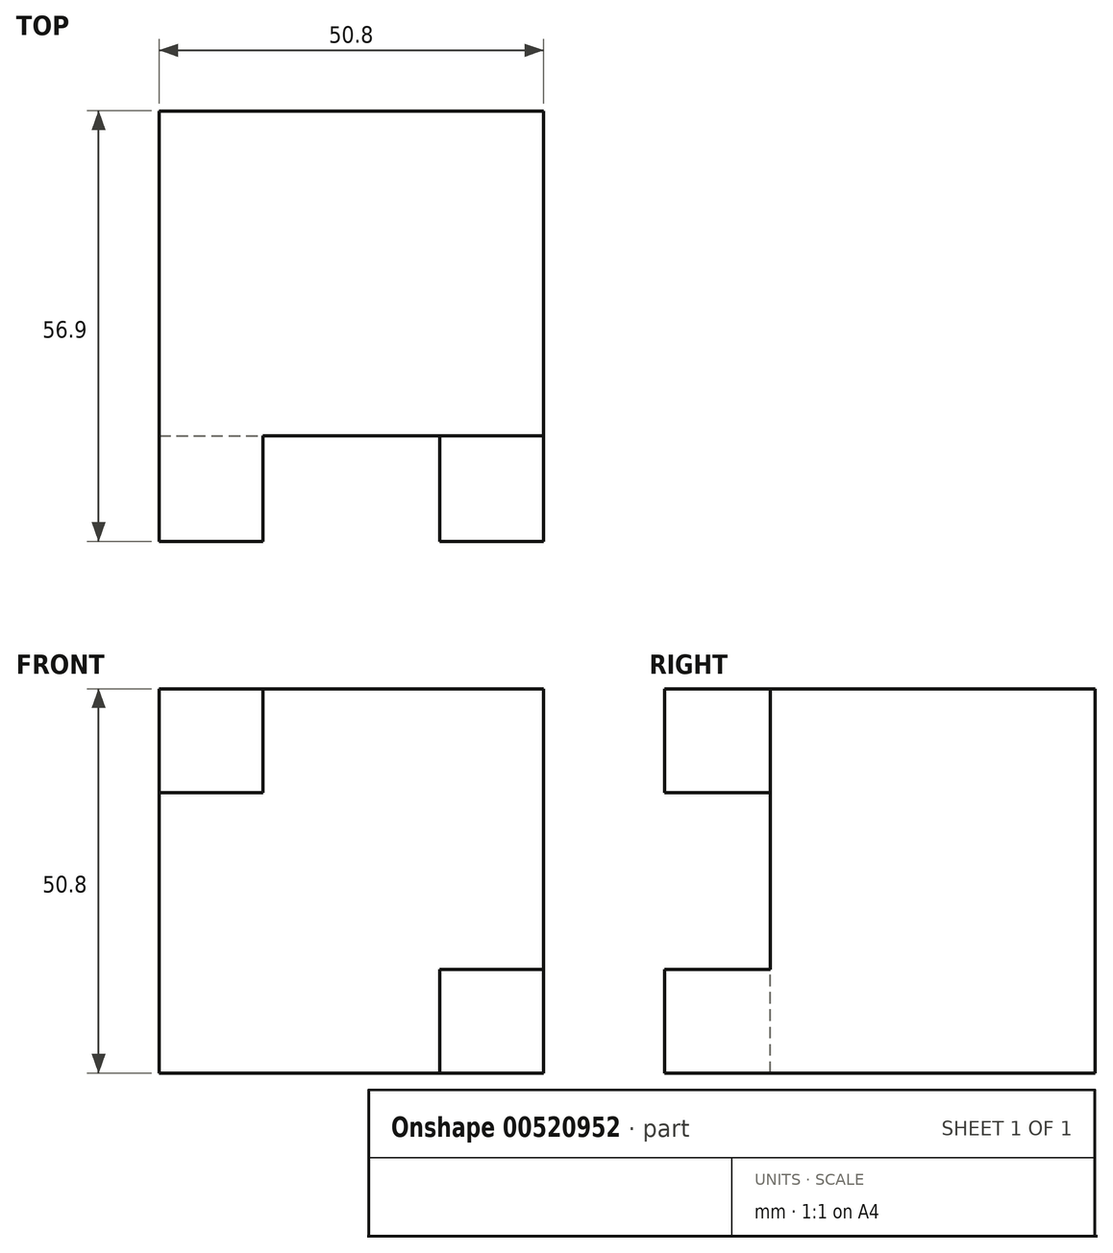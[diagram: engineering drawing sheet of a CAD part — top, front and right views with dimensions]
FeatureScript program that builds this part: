
annotation { "Feature Type Name" : "Feature", "Feature Type Description" : "" }
export const myFeature = defineFeature(function(context is Context, id is Id, definition is map)
    precondition{}
    {
        {
            var Q0;
            Q0=qCreatedBy(makeId("Front.planeOp"),FACE);
            var sketch = newSketch(context, id + "F0", { "sketchPlane" : qUnion([Q0])});
            skLineSegment(sketch, "E0.bottom", {"start": v(0, 0) * mm, "end": v(-50.8, 0) * mm});
            skLineSegment(sketch, "E0.top", {"start": v(0, 50.8) * mm, "end": v(-50.8, 50.8) * mm});
            skLineSegment(sketch, "E0.left", {"start": v(0, 0) * mm, "end": v(0, 50.8) * mm});
            skLineSegment(sketch, "E0.right", {"start": v(-50.8, 0) * mm, "end": v(-50.8, 50.8) * mm});
            skSolve(sketch);
        }
        {
            var Q0;
            Q0=makeQuery(id+"F0.imprint","IMPRINT",FACE,{"disambiguationData":[TD([[makeQuery(id+"F0.imprint","IMPRINT",EDGE,{"derivedFrom":sQuery(id+"F0.wireOp",EDGE,"E0.bottom")}),-1.0]])]});
            extrude(context, id + "F1", {"entities" : qUnion([Q0]), "oppositeDirection" : true, "depth" : 24.9 * mm, "offsetDistance" : 25.4 * mm});
        }
        {
            var Q0;
            Q0=makeQuery(id+"F1.opExtrude","CAP_FACE",FACE,{"disambiguationData":[OSD([sQuery(id+"F0.wireOp",EDGE,"E0.bottom"),sQuery(id+"F0.wireOp",EDGE,"E0.top"),sQuery(id+"F0.wireOp",EDGE,"E0.left"),sQuery(id+"F0.wireOp",EDGE,"E0.right")])],"isStart":true});
            var sketch = newSketch(context, id + "F2", { "sketchPlane" : qUnion([Q0])});
            skLineSegment(sketch, "E1.bottom", {"start": v(-50.8, 50.8) * mm, "end": v(-37.08, 50.8) * mm});
            skLineSegment(sketch, "E1.top", {"start": v(-50.8, 37.08) * mm, "end": v(-37.08, 37.08) * mm});
            skLineSegment(sketch, "E1.left", {"start": v(-50.8, 50.8) * mm, "end": v(-50.8, 37.08) * mm});
            skLineSegment(sketch, "E1.right", {"start": v(-37.08, 50.8) * mm, "end": v(-37.08, 37.08) * mm});
            skLineSegment(sketch, "E2.bottom", {"start": v(0, 0) * mm, "end": v(-13.72, 0) * mm});
            skLineSegment(sketch, "E2.top", {"start": v(0, 13.72) * mm, "end": v(-13.72, 13.72) * mm});
            skLineSegment(sketch, "E2.left", {"start": v(0, 0) * mm, "end": v(0, 13.72) * mm});
            skLineSegment(sketch, "E2.right", {"start": v(-13.72, 0) * mm, "end": v(-13.72, 13.72) * mm});
            skSolve(sketch);
        }
        {
            var Q0;
            Q0=makeQuery(id+"F2.imprint","IMPRINT",FACE,{"disambiguationData":[TD([[makeQuery(id+"F2.imprint","IMPRINT",EDGE,{"derivedFrom":sQuery(id+"F2.wireOp",EDGE,"E1.bottom")}),1.0]])]});
            var Q1;
            Q1=makeQuery(id+"F2.imprint","IMPRINT",FACE,{"disambiguationData":[TD([[makeQuery(id+"F2.imprint","IMPRINT",EDGE,{"derivedFrom":sQuery(id+"F2.wireOp",EDGE,"E2.bottom")}),-1.0]])]});
            extrude(context, id + "F3", {"entities" : qUnion([Q0, Q1]), "operationType" : NewBodyOperationType.ADD, "depth" : 13.97 * mm, "offsetDistance" : 25.4 * mm});
        }
        {
            var Q0;
            Q0=makeQuery(id+"F1.opExtrude","CAP_FACE",FACE,{"disambiguationData":[OSD([sQuery(id+"F0.wireOp",EDGE,"E0.bottom"),sQuery(id+"F0.wireOp",EDGE,"E0.top"),sQuery(id+"F0.wireOp",EDGE,"E0.left"),sQuery(id+"F0.wireOp",EDGE,"E0.right")])],"isStart":false});
            var sketch = newSketch(context, id + "F4", { "sketchPlane" : qUnion([Q0])});
            skLineSegment(sketch, "E3.bottom", {"start": v(50.8, 0) * mm, "end": v(37.08, 0) * mm});
            skLineSegment(sketch, "E3.top", {"start": v(50.8, 13.55) * mm, "end": v(37.08, 13.55) * mm});
            skLineSegment(sketch, "E3.left", {"start": v(50.8, 0) * mm, "end": v(50.8, 13.55) * mm});
            skLineSegment(sketch, "E3.right", {"start": v(37.08, 0) * mm, "end": v(37.08, 13.55) * mm});
            skLineSegment(sketch, "E4.bottom", {"start": v(50.8, 50.8) * mm, "end": v(37.08, 50.8) * mm});
            skLineSegment(sketch, "E4.top", {"start": v(50.8, 36.31) * mm, "end": v(37.08, 36.31) * mm});
            skLineSegment(sketch, "E4.left", {"start": v(50.8, 50.8) * mm, "end": v(50.8, 36.31) * mm});
            skLineSegment(sketch, "E4.right", {"start": v(37.08, 50.8) * mm, "end": v(37.08, 36.31) * mm});
            skLineSegment(sketch, "E5.bottom", {"start": v(0, 0) * mm, "end": v(13.72, 0) * mm});
            skLineSegment(sketch, "E5.top", {"start": v(0, 12.96) * mm, "end": v(13.72, 12.96) * mm});
            skLineSegment(sketch, "E5.left", {"start": v(0, 0) * mm, "end": v(0, 12.96) * mm});
            skLineSegment(sketch, "E5.right", {"start": v(13.72, 0) * mm, "end": v(13.72, 12.96) * mm});
            skLineSegment(sketch, "E6.bottom", {"start": v(0, 50.8) * mm, "end": v(13.72, 50.8) * mm});
            skLineSegment(sketch, "E6.top", {"start": v(0, 35.15) * mm, "end": v(13.72, 35.15) * mm});
            skLineSegment(sketch, "E6.left", {"start": v(0, 50.8) * mm, "end": v(0, 35.15) * mm});
            skLineSegment(sketch, "E6.right", {"start": v(13.72, 50.8) * mm, "end": v(13.72, 35.15) * mm});
            skSolve(sketch);
        }
        {
            var Q0;
            Q0=makeQuery(id+"F1.opExtrude","CAP_FACE",FACE,{"disambiguationData":[OSD([sQuery(id+"F0.wireOp",EDGE,"E0.bottom"),sQuery(id+"F0.wireOp",EDGE,"E0.top"),sQuery(id+"F0.wireOp",EDGE,"E0.left"),sQuery(id+"F0.wireOp",EDGE,"E0.right")])],"isStart":false});
            var sketch = newSketch(context, id + "F5", { "sketchPlane" : qUnion([Q0])});
            skSolve(sketch);
        }
        {
            var Q0;
            Q0=makeQuery(id+"F5.imprint","IMPRINT",FACE,{"disambiguationData":[TD([[makeQuery(id+"F5.imprint","IMPRINT",EDGE,{"derivedFrom":makeQuery(id+"F1.opExtrude","CAP_EDGE",EDGE,{"disambiguationData":[OSD([sQuery(id+"F0.wireOp",EDGE,"E0.bottom")])],"isStart":false})}),1.0]])]});
            var Q1;
            {var subQ6=sQuery(id+"F4.wireOp",EDGE,"E3.top");Q1=makeQuery(id+"F4.imprint","IMPRINT",FACE,{"disambiguationData":[TD([[makeQuery(id+"F4.imprint","IMPRINT",EDGE,{"derivedFrom":subQ6}),-1.0]])]});}
            var Q2;
            Q2=makeQuery(id+"F1.opExtrude","CAP_FACE",FACE,{"disambiguationData":[OSD([sQuery(id+"F0.wireOp",EDGE,"E0.bottom"),sQuery(id+"F0.wireOp",EDGE,"E0.top"),sQuery(id+"F0.wireOp",EDGE,"E0.left"),sQuery(id+"F0.wireOp",EDGE,"E0.right")])],"isStart":false});
            extrude(context, id + "F6", {"entities" : qUnion([Q0, Q1, Q2]), "operationType" : NewBodyOperationType.ADD, "endBound" : BoundingType.SYMMETRIC, "depth" : 36.07 * mm, "offsetDistance" : 25.4 * mm});
        }
    });
